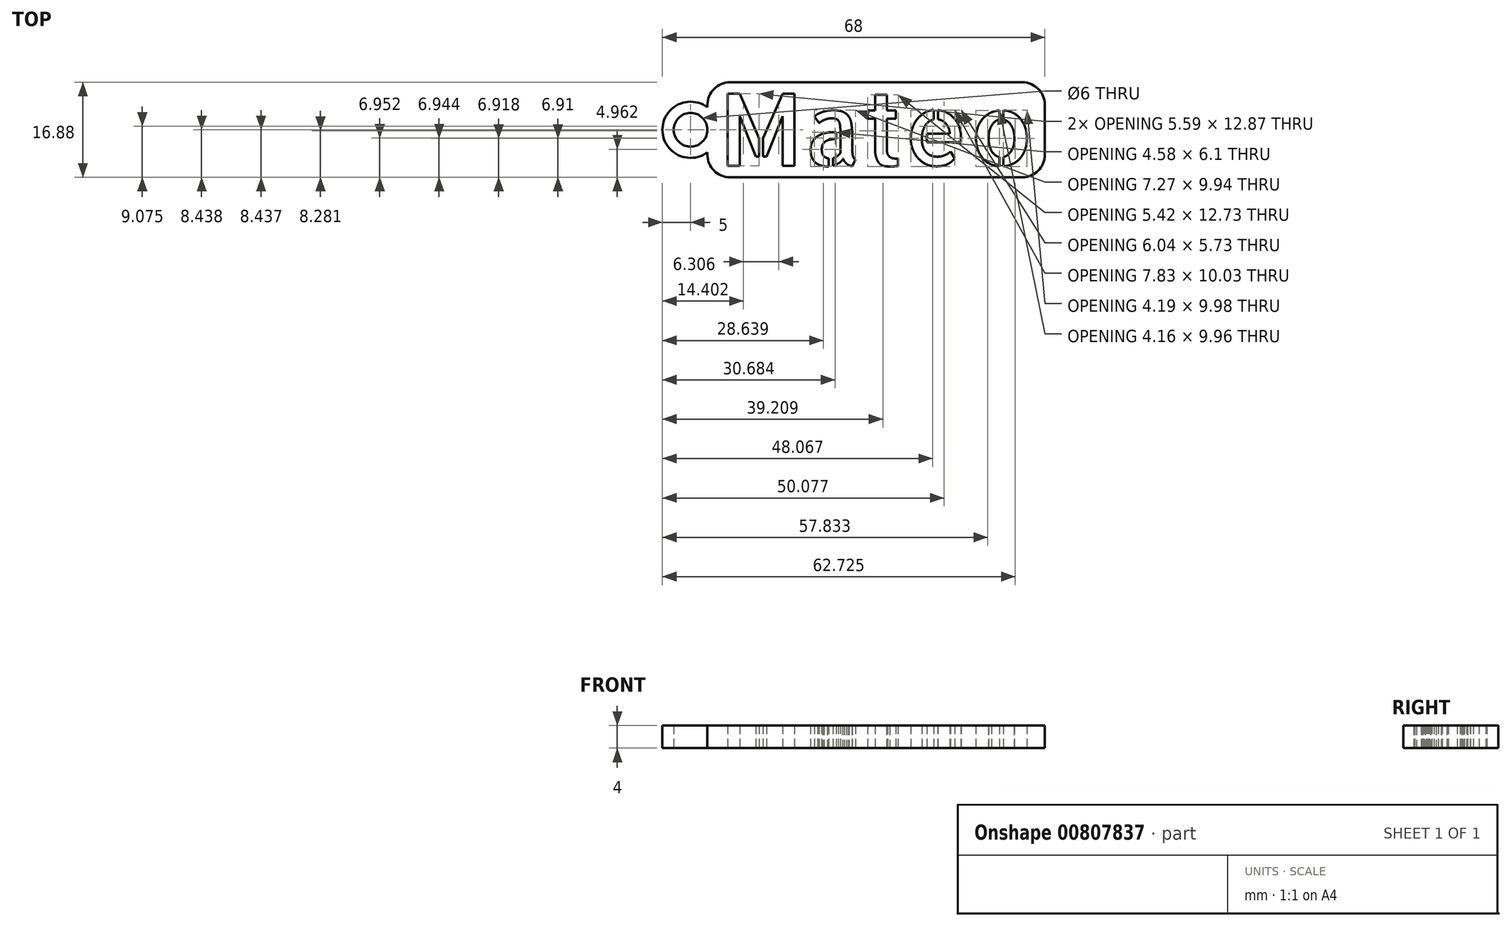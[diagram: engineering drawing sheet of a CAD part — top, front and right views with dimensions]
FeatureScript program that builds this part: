
annotation { "Feature Type Name" : "Feature", "Feature Type Description" : "" }
export const myFeature = defineFeature(function(context is Context, id is Id, definition is map)
    precondition{}
    {
        {
            var Q0;
            Q0=qCreatedBy(makeId("Top.planeOp"),FACE);
            var sketch = newSketch(context, id + "F0", { "sketchPlane" : qUnion([Q0])});
            skLineSegment(sketch, "E0.bottom", {"start": v(-2, -2) * mm, "end": v(58, -2) * mm});
            skLineSegment(sketch, "E0.top", {"start": v(-2, 14.88) * mm, "end": v(58, 14.88) * mm});
            skLineSegment(sketch, "E0.left", {"start": v(-2, -2) * mm, "end": v(-2, 2.44) * mm});
            skLineSegment(sketch, "E0.right", {"start": v(58, -2) * mm, "end": v(58, 14.88) * mm});
            skArc(sketch, "E1", {"start": v(-2, 10.44) * mm, "mid": v(-10, 6.44) * mm, "end": v(-2, 2.44) * mm});
            skLineSegment(sketch, "E2.trimOffspring", {"start": v(-2, 10.44) * mm, "end": v(-2, 14.88) * mm});
            skCircle(sketch, "E3", {"center": v(-5, 6.44) * mm, "radius": 3 * mm});
            skLineSegment(sketch, "E4", {"start": v(58, 6.44) * mm, "end": v(-10, 6.44) * mm, "construction": true});
            skText(sketch, "E5", { "text": "Mateo", "fontName": "AllertaStencil-Regular.ttf"});
            const initialGuessF0  = {"E5": [0, 0, 1, 0, 0.01288]};
            skSetInitialGuess(sketch, initialGuessF0);
            skSolve(sketch);
        }
        {
            var Q0;
            Q0=makeQuery(id+"F0.imprint","IMPRINT",FACE,{"disambiguationData":[TD([[makeQuery(id+"F0.imprint","IMPRINT",EDGE,{"derivedFrom":sQuery(id+"F0.wireOp",EDGE,"E0.bottom")}),1.0]])]});
            extrude(context, id + "F1", {"entities" : qUnion([Q0]), "depth" : 4 * mm, "offsetDistance" : 25 * mm});
        }
        {
            var Q0;
            Q0=makeQuery(id+"F1.opExtrude","SWEPT_EDGE",EDGE,{"disambiguationData":[OSD([sQuery(id+"F0.wireOp",EDGE,"E0.bottom"),sQuery(id+"F0.wireOp",EDGE,"E0.left")])]});
            var Q1;
            Q1=makeQuery(id+"F1.opExtrude","SWEPT_EDGE",EDGE,{"disambiguationData":[OSD([sQuery(id+"F0.wireOp",EDGE,"E0.bottom"),sQuery(id+"F0.wireOp",EDGE,"E0.right")])]});
            var Q2;
            Q2=makeQuery(id+"F1.opExtrude","SWEPT_EDGE",EDGE,{"disambiguationData":[OSD([sQuery(id+"F0.wireOp",EDGE,"E0.top"),sQuery(id+"F0.wireOp",EDGE,"E0.right")])]});
            var Q3;
            Q3=makeQuery(id+"F1.opExtrude","SWEPT_EDGE",EDGE,{"disambiguationData":[OSD([sQuery(id+"F0.wireOp",EDGE,"E0.top"),sQuery(id+"F0.wireOp",EDGE,"E2.trimOffspring")])]});
            fillet(context, id + "F2", {"entities" : qUnion([Q0, Q1, Q2, Q3]), "radius" : 4 * mm, "tangentPropagation" : true, "allowEdgeOverflow" : false});
        }
    });
